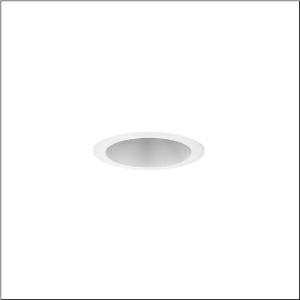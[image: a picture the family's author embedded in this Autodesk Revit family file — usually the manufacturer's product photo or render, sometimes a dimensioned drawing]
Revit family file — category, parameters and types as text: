
# Revit family: lunis_31-l_51dn16me31b
name_source: partatom
category: Lighting Fixtures
units: mm (PartAtom-declared; Revit-internal decimal feet)

## family parameters
Cut with Voids When Loaded = No
Host = Face
Light Source = No
Part Type = Normal
Room Calculation Point = No
Round Connector Dimension = Use Diameter
Shared = No

## types (1)
- --- (1 x LED, 1600 lm, 11.5 W, 3000K)
    Apparent Load = 12 VA
    CIE Flux Codes = 76 93 99 100 100
    Color Rendering = 80
    Color Temperature = 3000K
    Default Elevation = 1800 mm
    Description = Lunis 31-L, downlight, light control with reflector, light emission: direct distribution, LED rated luminous flux: 1.600lm, light colour: 830, mains connection: 220..240V, AC/DC, 0/50..60Hz, housing, of aluminium, white, protection rating (complete): IP20, protection rating (on room side): IP54, insulation class (complete): insulation class II (safety insulation), certification: CE, ENEC, packaging unit: 1 piece
    Height = 0 mm  [stored 0 ft]
    Lamp = 1 x LED
    Lamp Light Flux = 1600 lm
    Lamp Power = 11.5 W
    Lamp count = 1
    Length = 188 mm  [stored 0.616798 ft]
    Luminous efficacy = 139 lm/W
    Manufacturer = Siteco
    ModVariant = No
    Model = 51DN16ME31B
    Mounting Place = Ceiling
    Mounting Type = Recessed
    Number of Poles = 1
    OnlyDefault = Yes
    Power Factor = 1
    Product Name = Lunis 31-L
    Product group = downlight
    ProductGroupID = 401
    Protection Class = Protection class II
    Protection Degree = IP 20
    RLX_Detail_Level = 1
    RLX_Emergency_Light_Flux = 0 lm
    RLX_Emergency_Type = 0
    RLX_Emergency_Type_DB = No
    RlxData = <blob elided: 22477 chars, md5=0670ea9d>
    Socket = socket
    Standby Power = 0 W
    System Light Flux = 1600 lm
    System Power = 12 W
    Type Comments = individual setting: luminous flux: 100 % | (OFF | ON) | 300 mA
    Type Image = l_1345911.jpg
    URL = http://relux.com
    VarID = @adj_031459
    Voltage = 0 V
    Weight = 0.00 kg
    Width = 0 mm  [stored 0 ft]

note: [stored X ft] marks values corroborated as IEEE doubles in the binary element streams (Revit-internal decimal feet)

## geometry (parser evidence)
native form markers: Blend x4, Sweep x10
no freeform markers — native parametric forms only
